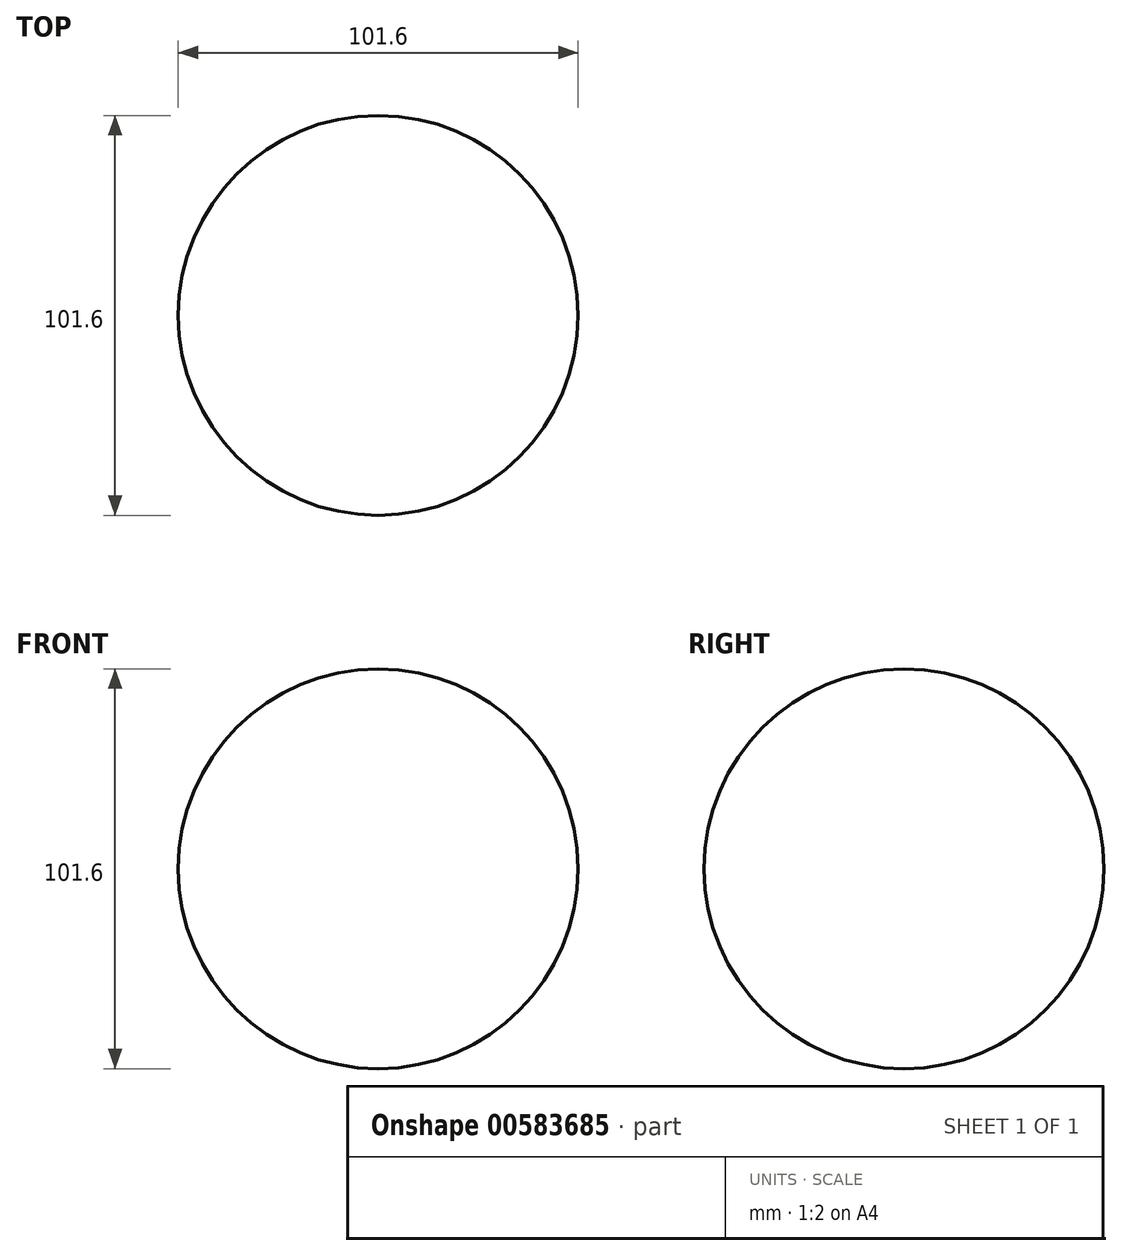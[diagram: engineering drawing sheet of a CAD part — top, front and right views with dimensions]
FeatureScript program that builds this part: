
annotation { "Feature Type Name" : "Feature", "Feature Type Description" : "" }
export const myFeature = defineFeature(function(context is Context, id is Id, definition is map)
    precondition{}
    {
        {
            var Q0;
            Q0=qCreatedBy(makeId("Front.planeOp"),FACE);
            var sketch = newSketch(context, id + "F0", { "sketchPlane" : qUnion([Q0])});
            skArc(sketch, "E0", {"start": v(-50.8, 0) * mm, "mid": v(0, 50.8) * mm, "end": v(50.8, 0) * mm});
            skLineSegment(sketch, "E1", {"start": v(-50.8, 0) * mm, "end": v(50.8, 0) * mm});
            skSolve(sketch);
        }
        {
            var Q0;
            Q0 = qSketchRegion(id + "F0", true);
            var Q1;
            Q1=sQuery(id+"F0.wireOp",EDGE,"E1");
            revolve(context, id + "F1", {"entities" : qUnion([Q0]), "axis" : qUnion([Q1]), "revolveType" : RevolveType.FULL});
        }
    });
